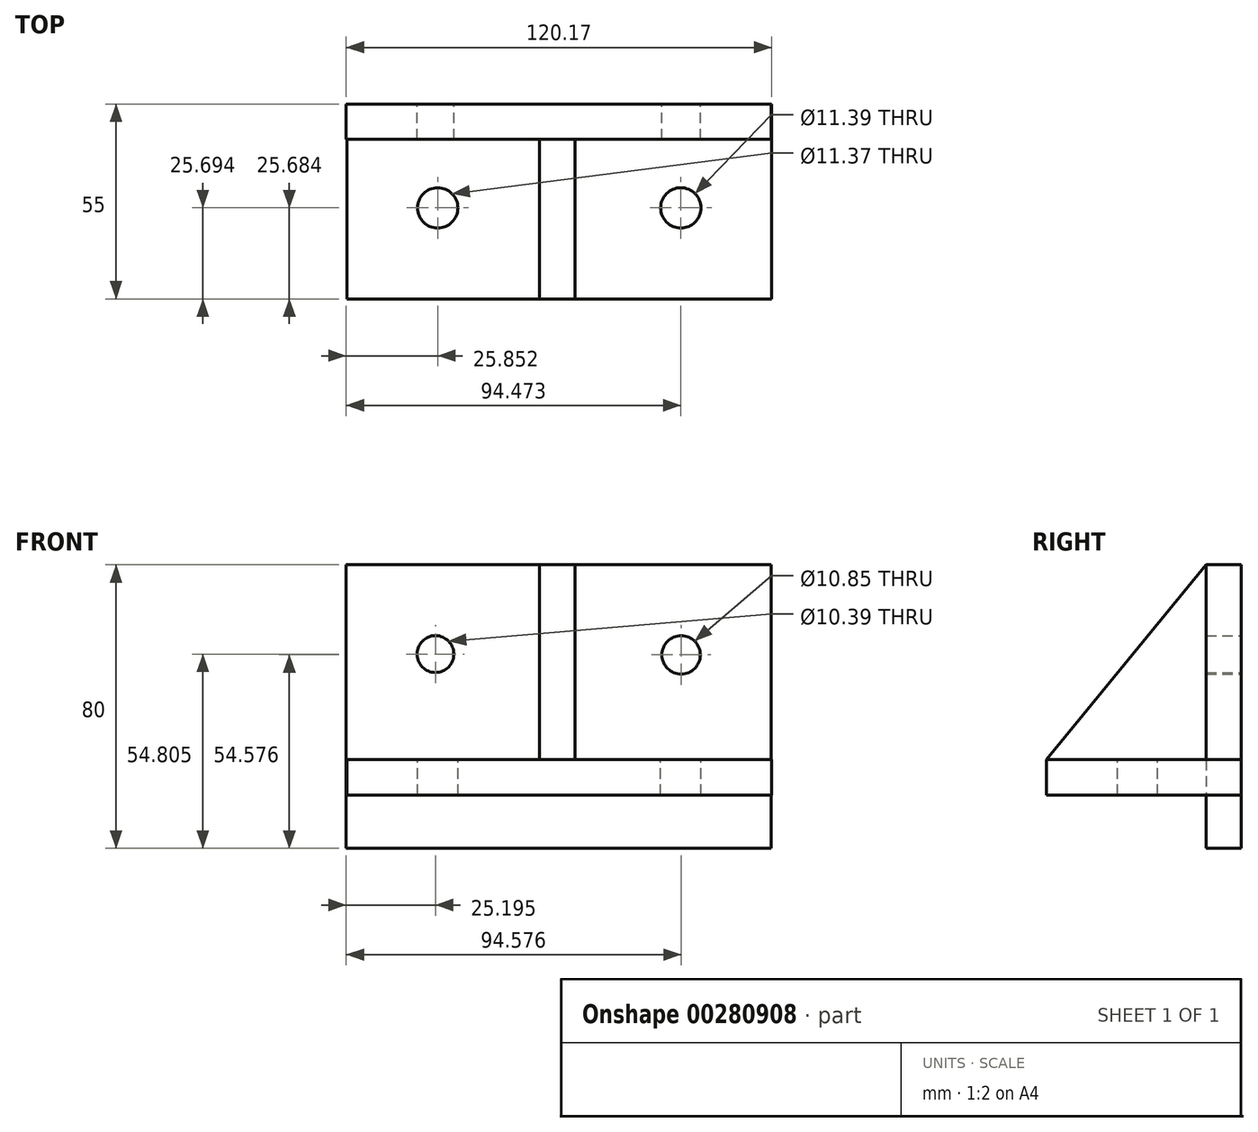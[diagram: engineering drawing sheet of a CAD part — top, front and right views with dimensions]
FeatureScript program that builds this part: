
annotation { "Feature Type Name" : "Feature", "Feature Type Description" : "" }
export const myFeature = defineFeature(function(context is Context, id is Id, definition is map)
    precondition{}
    {
        {
            var Q0;
            Q0=qCreatedBy(makeId("Front.planeOp"),FACE);
            var sketch = newSketch(context, id + "F0", { "sketchPlane" : qUnion([Q0])});
            skLineSegment(sketch, "E0.bottom", {"start": v(-60, -40) * mm, "end": v(60, -40) * mm});
            skLineSegment(sketch, "E0.top", {"start": v(-60, 40) * mm, "end": v(60, 40) * mm});
            skLineSegment(sketch, "E0.left", {"start": v(-60, -40) * mm, "end": v(-60, 40) * mm});
            skLineSegment(sketch, "E0.right", {"start": v(60, -40) * mm, "end": v(60, 40) * mm});
            skPoint(sketch, "E0.middle", {"position": v(0, 0) * mm});
            skCircle(sketch, "E1", {"center": v(34.58, 14.58) * mm, "radius": 5.42 * mm});
            skCircle(sketch, "E2", {"center": v(-34.8, 14.8) * mm, "radius": 5.2 * mm});
            skSolve(sketch);
        }
        {
            var Q0;
            Q0 = qSketchRegion(id + "F0", true);
            extrude(context, id + "F1", {"entities" : qUnion([Q0]), "depth" : 10 * mm});
        }
        {
            var Q0;
            Q0=qCreatedBy(makeId("Front.planeOp"),FACE);
            var sketch = newSketch(context, id + "F2", { "sketchPlane" : qUnion([Q0])});
            skLineSegment(sketch, "E3.bottom", {"start": v(-59.83, -25) * mm, "end": v(60.17, -25) * mm});
            skLineSegment(sketch, "E3.top", {"start": v(-59.83, -15) * mm, "end": v(60.17, -15) * mm});
            skLineSegment(sketch, "E3.left", {"start": v(-59.83, -25) * mm, "end": v(-59.83, -15) * mm});
            skLineSegment(sketch, "E3.right", {"start": v(60.17, -25) * mm, "end": v(60.17, -15) * mm});
            skSolve(sketch);
        }
        {
            var Q0;
            Q0 = qSketchRegion(id + "F2", true);
            extrude(context, id + "F3", {"entities" : qUnion([Q0]), "operationType" : NewBodyOperationType.ADD, "depth" : 55 * mm});
        }
        {
            var Q0;
            Q0=makeQuery(id+"F3.opExtrude","SWEPT_FACE",FACE,{"disambiguationData":[OSD([sQuery(id+"F2.wireOp",EDGE,"E3.top")])]});
            var sketch = newSketch(context, id + "F4", { "sketchPlane" : qUnion([Q0])});
            skCircle(sketch, "E4", {"center": v(-34.15, -29.32) * mm, "radius": 5.68 * mm});
            skCircle(sketch, "E5", {"center": v(34.47, -29.3) * mm, "radius": 5.7 * mm});
            skSolve(sketch);
        }
        {
            var Q0;
            Q0 = qSketchRegion(id + "F4", true);
            extrude(context, id + "F5", {"entities" : qUnion([Q0]), "operationType" : NewBodyOperationType.REMOVE, "oppositeDirection" : true, "depth" : 10 * mm});
        }
        {
            var Q0;
            Q0=makeQuery(id+"F3.opExtrude","SWEPT_FACE",FACE,{"disambiguationData":[OSD([sQuery(id+"F2.wireOp",EDGE,"E3.top")])]});
            var sketch = newSketch(context, id + "F6", { "sketchPlane" : qUnion([Q0])});
            skLineSegment(sketch, "E6.bottom", {"start": v(-5.44, -10) * mm, "end": v(4.56, -10) * mm});
            skLineSegment(sketch, "E6.top", {"start": v(-5.44, -55) * mm, "end": v(4.56, -55) * mm});
            skLineSegment(sketch, "E6.left", {"start": v(-5.44, -10) * mm, "end": v(-5.44, -55) * mm});
            skLineSegment(sketch, "E6.right", {"start": v(4.56, -10) * mm, "end": v(4.56, -55) * mm});
            skSolve(sketch);
        }
        {
            var Q0;
            Q0 = qSketchRegion(id + "F6", true);
            extrude(context, id + "F7", {"entities" : qUnion([Q0]), "operationType" : NewBodyOperationType.ADD, "depth" : 55 * mm});
        }
        {
            var Q0;
            Q0=makeQuery(id+"F7.opExtrude","SWEPT_FACE",FACE,{"disambiguationData":[OSD([sQuery(id+"F6.wireOp",EDGE,"E6.right")])]});
            var sketch = newSketch(context, id + "F8", { "sketchPlane" : qUnion([Q0])});
            skLineSegment(sketch, "E7", {"start": v(-10, 40) * mm, "end": v(-55, 40) * mm});
            skLineSegment(sketch, "E8", {"start": v(-55, 40) * mm, "end": v(-55, -15) * mm});
            skLineSegment(sketch, "E9", {"start": v(-55, -15) * mm, "end": v(-10, 40) * mm});
            skSolve(sketch);
        }
        {
            var Q0;
            Q0 = qSketchRegion(id + "F8", true);
            extrude(context, id + "F9", {"entities" : qUnion([Q0]), "operationType" : NewBodyOperationType.REMOVE, "oppositeDirection" : true, "depth" : 25 * mm});
        }
    });
